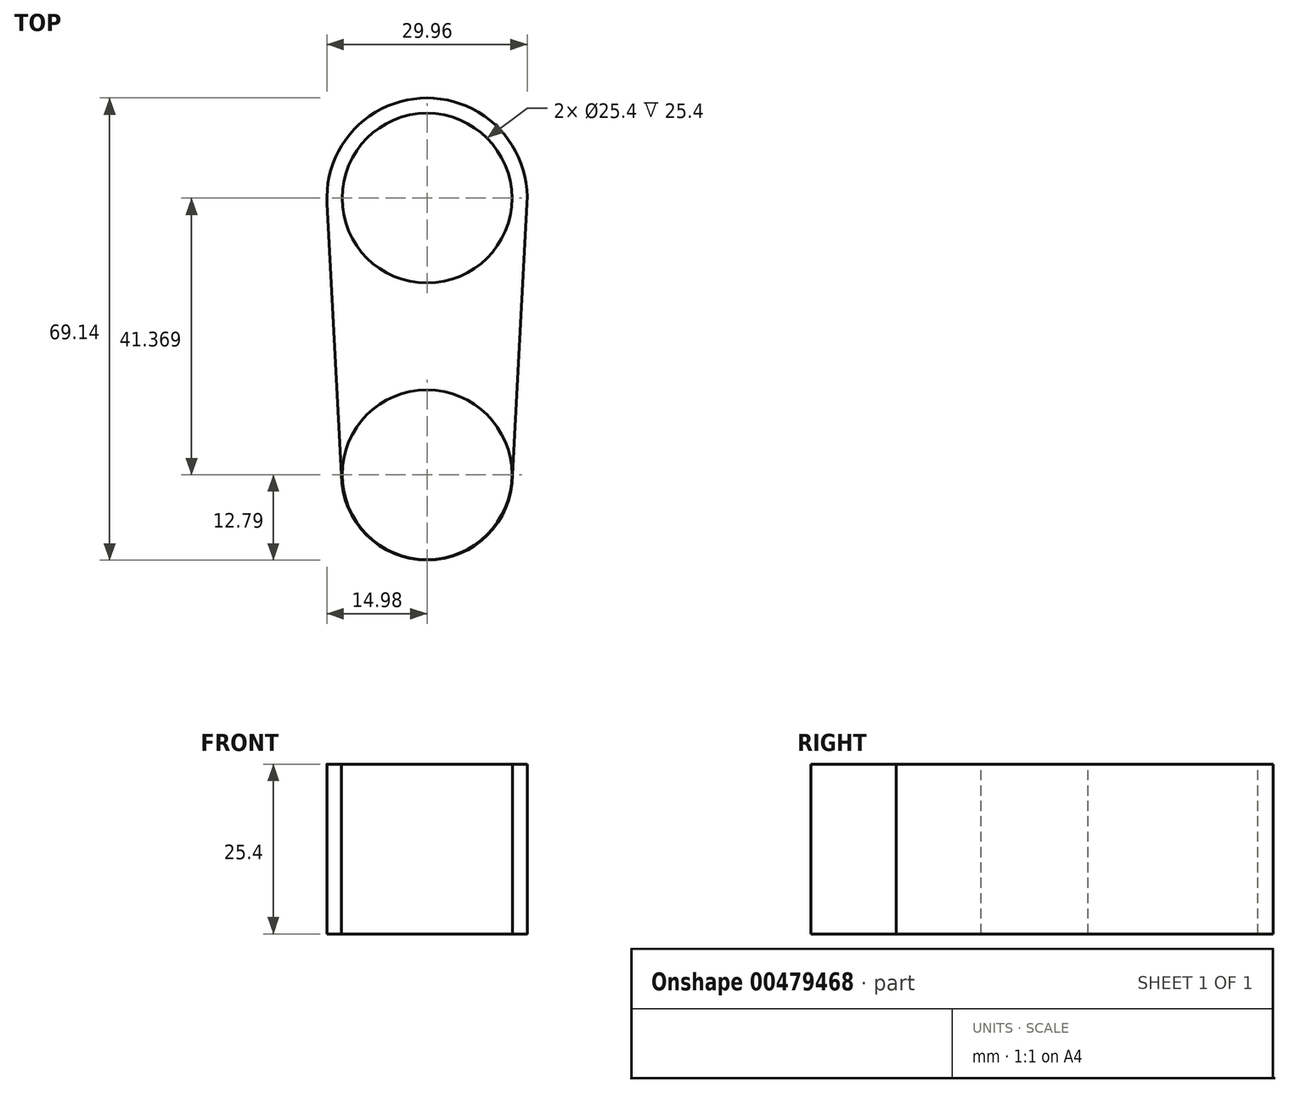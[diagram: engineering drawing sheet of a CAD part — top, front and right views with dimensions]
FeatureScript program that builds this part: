
annotation { "Feature Type Name" : "Feature", "Feature Type Description" : "" }
export const myFeature = defineFeature(function(context is Context, id is Id, definition is map)
    precondition{}
    {
        {
            var Q0;
            Q0=qCreatedBy(makeId("Top.planeOp"),FACE);
            var sketch = newSketch(context, id + "F0", { "sketchPlane" : qUnion([Q0])});
            skCircle(sketch, "E0", {"center": v(0, 41.37) * mm, "radius": 14.98 * mm});
            skCircle(sketch, "E1", {"center": v(0, 0) * mm, "radius": 12.79 * mm});
            skLineSegment(sketch, "E2", {"start": v(-12.79, 0) * mm, "end": v(-14.96, 40.57) * mm});
            skLineSegment(sketch, "E3", {"start": v(12.79, 0) * mm, "end": v(14.96, 40.57) * mm});
            skSolve(sketch);
        }
        {
            var Q0;
            {var subQ0=sQuery(id+"F0.wireOp",EDGE,"E2");Q0=makeQuery(id+"F0.imprint","IMPRINT",FACE,{"disambiguationData":[TD([[makeQuery(id+"F0.imprint","IMPRINT",EDGE,{"derivedFrom":subQ0}),-1.0]])]});}
            var Q1;
            {var subQ0=sQuery(id+"F0.wireOp",EDGE,"E0");var subQ1=makeQuery(id+"F0.imprint","INTERSECT",VERTEX,{"derivedFrom":[subQ0,sQuery(id+"F0.wireOp",EDGE,"E2")]});Q1=makeQuery(id+"F0.imprint","IMPRINT",FACE,{"disambiguationData":[TD([[makeQuery(id+"F0.imprint","IMPRINT",EDGE,{"disambiguationData":[TD([[subQ1,-1.0]])],"derivedFrom":subQ0}),1.0]])]});}
            var Q2;
            {var subQ0=sQuery(id+"F0.wireOp",EDGE,"E1");var subQ1=makeQuery(id+"F0.imprint","INTERSECT",VERTEX,{"derivedFrom":[subQ0,sQuery(id+"F0.wireOp",EDGE,"E2")]});Q2=makeQuery(id+"F0.imprint","IMPRINT",FACE,{"disambiguationData":[TD([[makeQuery(id+"F0.imprint","IMPRINT",EDGE,{"disambiguationData":[TD([[subQ1,1.0]])],"derivedFrom":subQ0}),1.0]])]});}
            extrude(context, id + "F1", {"entities" : qUnion([Q0, Q1, Q2]), "depth" : 25.4 * mm});
        }
        {
            var Q0;
            Q0=makeQuery(id+"F1.opExtrude","CAP_FACE",FACE,{"disambiguationData":[OSD([sQuery(id+"F0.wireOp",EDGE,"E0"),sQuery(id+"F0.wireOp",EDGE,"E1"),sQuery(id+"F0.wireOp",EDGE,"E2"),sQuery(id+"F0.wireOp",EDGE,"E3")])],"isStart":false});
            var sketch = newSketch(context, id + "F2", { "sketchPlane" : qUnion([Q0])});
            skCircle(sketch, "E4", {"center": v(0, 41.37) * mm, "radius": 10.65 * mm});
            skCircle(sketch, "E5", {"center": v(0, 0) * mm, "radius": 8.85 * mm});
            skSolve(sketch);
        }
        {
            var Q0;
            Q0=sQuery(id+"F2.wireOp",VERTEX,"E5.center");
            var Q1;
            Q1=sQuery(id+"F2.wireOp",VERTEX,"E4.center");
            var Q2;
            Q2=makeQuery(id+"F1.opExtrude","SWEPT_BODY",BODY,{"disambiguationData":[OSD([sQuery(id+"F0.wireOp",EDGE,"E0"),sQuery(id+"F0.wireOp",EDGE,"E1"),sQuery(id+"F0.wireOp",EDGE,"E2"),sQuery(id+"F0.wireOp",EDGE,"E3")])]});
            hole(context, id + "F3", {"style" : HoleStyle.SIMPLE, "endStyle" : HoleEndStyle.THROUGH, "holeDiameter" : 25.4 * mm, "isTappedThrough" : true, "tappedDepth" : 12.7 * mm, "tapClearance" : 3, "locations" : qUnion([Q0, Q1]), "scope" : qUnion([Q2])});
        }
    });
